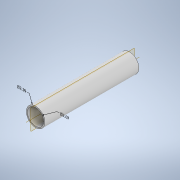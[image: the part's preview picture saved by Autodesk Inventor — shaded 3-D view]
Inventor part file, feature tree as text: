
AUTODESK INVENTOR PART (.ipt)
format: ipt  version: 2022.2 (Build 262287000, 287)  size: 110,592 bytes
history: native  units: in
note: dims shown in document units (in); Inventor stores cm internally (conversion verified against a paired STEP export)
features: other x3, extrude x1, sketch x1
ambient origin geometry x8: Origin, YZ Plane, XZ Plane, XY Plane, X Axis, Y Axis, Z Axis, Center Point
bodies: Solid1 (feature_tree)
feature tree (5):
  other  "Annotations"
  extrude  "Extrusion1"  Depth=12.0in
  sketch  "Sketch1"  dims[d0=2.385in d1=2.067in d2=12.0in d3=0.0in d4=0.7589in d5=2.385in d6=0.244in d7=2.067in]
  other  "Diameter Dimension 1"
  other  "Diameter Dimension 2"
